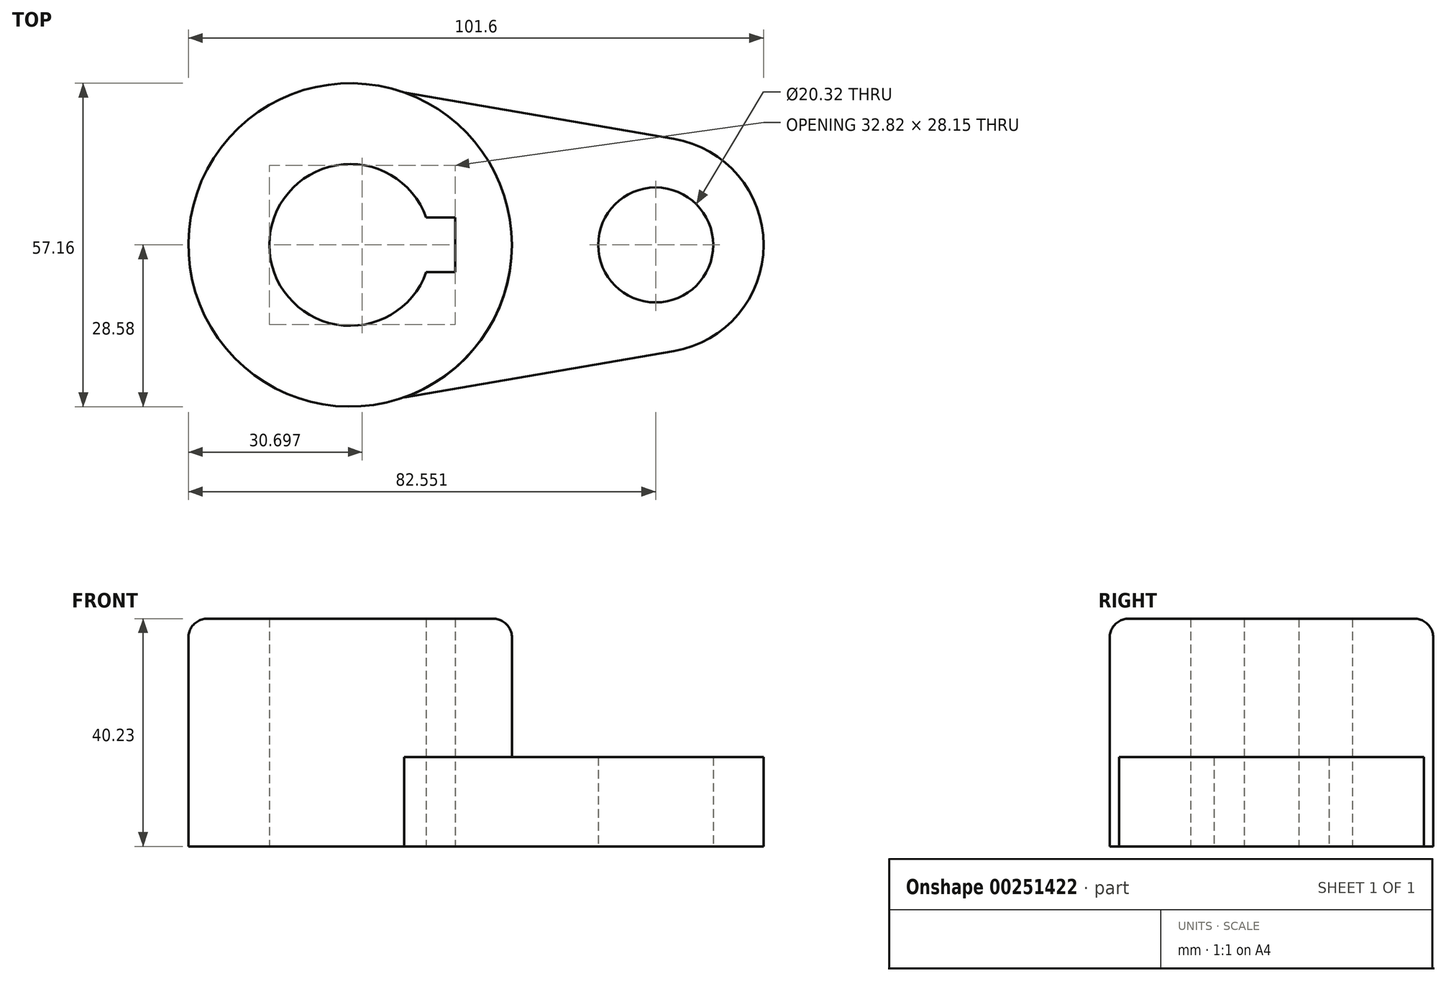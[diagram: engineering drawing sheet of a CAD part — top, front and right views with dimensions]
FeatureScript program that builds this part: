
annotation { "Feature Type Name" : "Feature", "Feature Type Description" : "" }
export const myFeature = defineFeature(function(context is Context, id is Id, definition is map)
    precondition{}
    {
        {
            var Q0;
            Q0=qCreatedBy(makeId("Top.planeOp"),FACE);
            var sketch = newSketch(context, id + "F0", { "sketchPlane" : qUnion([Q0])});
            skArc(sketch, "E0", {"start": v(-15.22, 4.83) * mm, "mid": v(-42.95, 0) * mm, "end": v(-15.22, -4.83) * mm});
            skCircle(sketch, "E1", {"center": v(25.31, 0) * mm, "radius": 10.16 * mm});
            skCircle(sketch, "E2", {"center": v(-28.66, 0) * mm, "radius": 28.58 * mm});
            skCircle(sketch, "E3", {"center": v(25.31, 0) * mm, "radius": 19.05 * mm});
            skPoint(sketch, "E4.visualSharp", {"position": v(33.04, -28.58) * mm});
            skLineSegment(sketch, "E5", {"start": v(-19.15, -26.95) * mm, "end": v(28.53, -18.78) * mm});
            skLineSegment(sketch, "E6", {"start": v(-19.15, 26.95) * mm, "end": v(28.53, 18.78) * mm});
            skLineSegment(sketch, "E7.right", {"start": v(-10.13, -4.83) * mm, "end": v(-10.13, 4.83) * mm});
            skLineSegment(sketch, "E8.trimOffspring", {"start": v(-15.22, 4.83) * mm, "end": v(-10.13, 4.83) * mm});
            skLineSegment(sketch, "E9.trimOffspring", {"start": v(-15.22, -4.83) * mm, "end": v(-10.13, -4.83) * mm});
            skPoint(sketch, "E10.orphan", {"position": v(-28.66, 28.58) * mm});
            skPoint(sketch, "E11.orphan", {"position": v(-28.66, -28.57) * mm});
            skSolve(sketch);
        }
        {
            var Q0;
            Q0=makeQuery(id+"F0.imprint","IMPRINT",FACE,{"disambiguationData":[TD([[makeQuery(id+"F0.imprint","IMPRINT",EDGE,{"derivedFrom":sQuery(id+"F0.wireOp",EDGE,"E0")}),-1.0]])]});
            extrude(context, id + "F1", {"entities" : qUnion([Q0]), "depth" : 40.23 * mm});
        }
        {
            var Q0;
            {var subQ0=sQuery(id+"F0.wireOp",EDGE,"E6");var subQ1=sQuery(id+"F0.wireOp",EDGE,"E2");var subQ2=makeQuery(id+"F0.imprint","INTERSECT",VERTEX,{"disambiguationData":[OD(1.0)],"derivedFrom":[subQ1,subQ0]});Q0=makeQuery(id+"F0.imprint","IMPRINT",FACE,{"disambiguationData":[TD([[makeQuery(id+"F0.imprint","IMPRINT",EDGE,{"disambiguationData":[TD([[subQ2,1.0]])],"derivedFrom":subQ1}),-1.0]])]});}
            var Q1;
            Q1=makeQuery(id+"F0.imprint","IMPRINT",FACE,{"disambiguationData":[TD([[makeQuery(id+"F0.imprint","IMPRINT",EDGE,{"derivedFrom":sQuery(id+"F0.wireOp",EDGE,"E1")}),-1.0]])]});
            extrude(context, id + "F2", {"entities" : qUnion([Q0, Q1]), "operationType" : NewBodyOperationType.ADD, "depth" : 15.77 * mm});
        }
        {
            var Q0;
            {var subQ0=sQuery(id+"F0.wireOp",EDGE,"E2");Q0=makeQuery(id+"F1.opExtrude","CAP_EDGE",EDGE,{"disambiguationData":[OSD([subQ0]),TDD([makeQuery(id+"F0.imprint","IMPRINT",EDGE,{"disambiguationData":[TD([[makeQuery(id+"F0.imprint","INTERSECT",VERTEX,{"disambiguationData":[OD(0.0)],"derivedFrom":[subQ0,sQuery(id+"F0.wireOp",EDGE,"E5")]}),1.0]])],"derivedFrom":subQ0})])],"isStart":false});}
            var Q1;
            Q1=makeQuery(id+"F1.opExtrude","CAP_EDGE",EDGE,{"disambiguationData":[OSD([sQuery(id+"F0.wireOp",EDGE,"E5")])],"isStart":false});
            var Q2;
            {var subQ0=sQuery(id+"F0.wireOp",EDGE,"E2");Q2=makeQuery(id+"F1.opExtrude","CAP_EDGE",EDGE,{"disambiguationData":[OSD([subQ0]),TDD([makeQuery(id+"F0.imprint","IMPRINT",EDGE,{"disambiguationData":[TD([[makeQuery(id+"F0.imprint","INTERSECT",VERTEX,{"disambiguationData":[OD(1.0)],"derivedFrom":[subQ0,sQuery(id+"F0.wireOp",EDGE,"E6")]}),1.0]])],"derivedFrom":subQ0})])],"isStart":false});}
            var Q3;
            Q3=makeQuery(id+"F1.opExtrude","CAP_EDGE",EDGE,{"disambiguationData":[OSD([sQuery(id+"F0.wireOp",EDGE,"E6")])],"isStart":false});
            fillet(context, id + "F3", {"entities" : qUnion([Q0, Q1, Q2, Q3]), "radius" : 3.3 * mm, "tangentPropagation" : true, "allowEdgeOverflow" : false});
        }
    });
